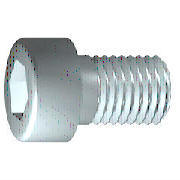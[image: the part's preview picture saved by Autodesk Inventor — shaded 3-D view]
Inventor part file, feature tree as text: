
AUTODESK INVENTOR PART (.ipt)
format: ipt  version: 2020 (Build 240168000, 168)  size: 188,928 bytes
history: native  units: mm (DEFAULTED — no unit token found)
features: sketch x2, extrude x1, plane x1, fillet x1
ambient origin geometry x7: Origin, YZ Plane, XY Plane, X Axis, Y Axis, Z Axis, Center Point
bodies: Solid1 (feature_tree), Body (feature_tree)
feature tree (5):
  extrude  "Slot"  Depth=3.0mm
  plane  "Work Plane1"
  fillet  "Fillet2"  Radius=3.0mm
  sketch  "Sketch1"  dims[d1=18.0mm d2=0.306825mm d3=3.0mm]
  sketch  "Sketch2"  dims[d4=1.3mm d5=60.0deg d6=3.0mm d7=3.0mm d8=2.886751mm d9=5.5mm d10=90.0deg d11=10.0mm d12=0.0mm d13=18.0mm d14=0.0mm d15=0.306725mm d16=0.306725mm d17=0.3mm d19=0.0mm d26=30.0mm d27=45.0deg d28=0.0mm d29=0.0mm d30=0.1mm]
